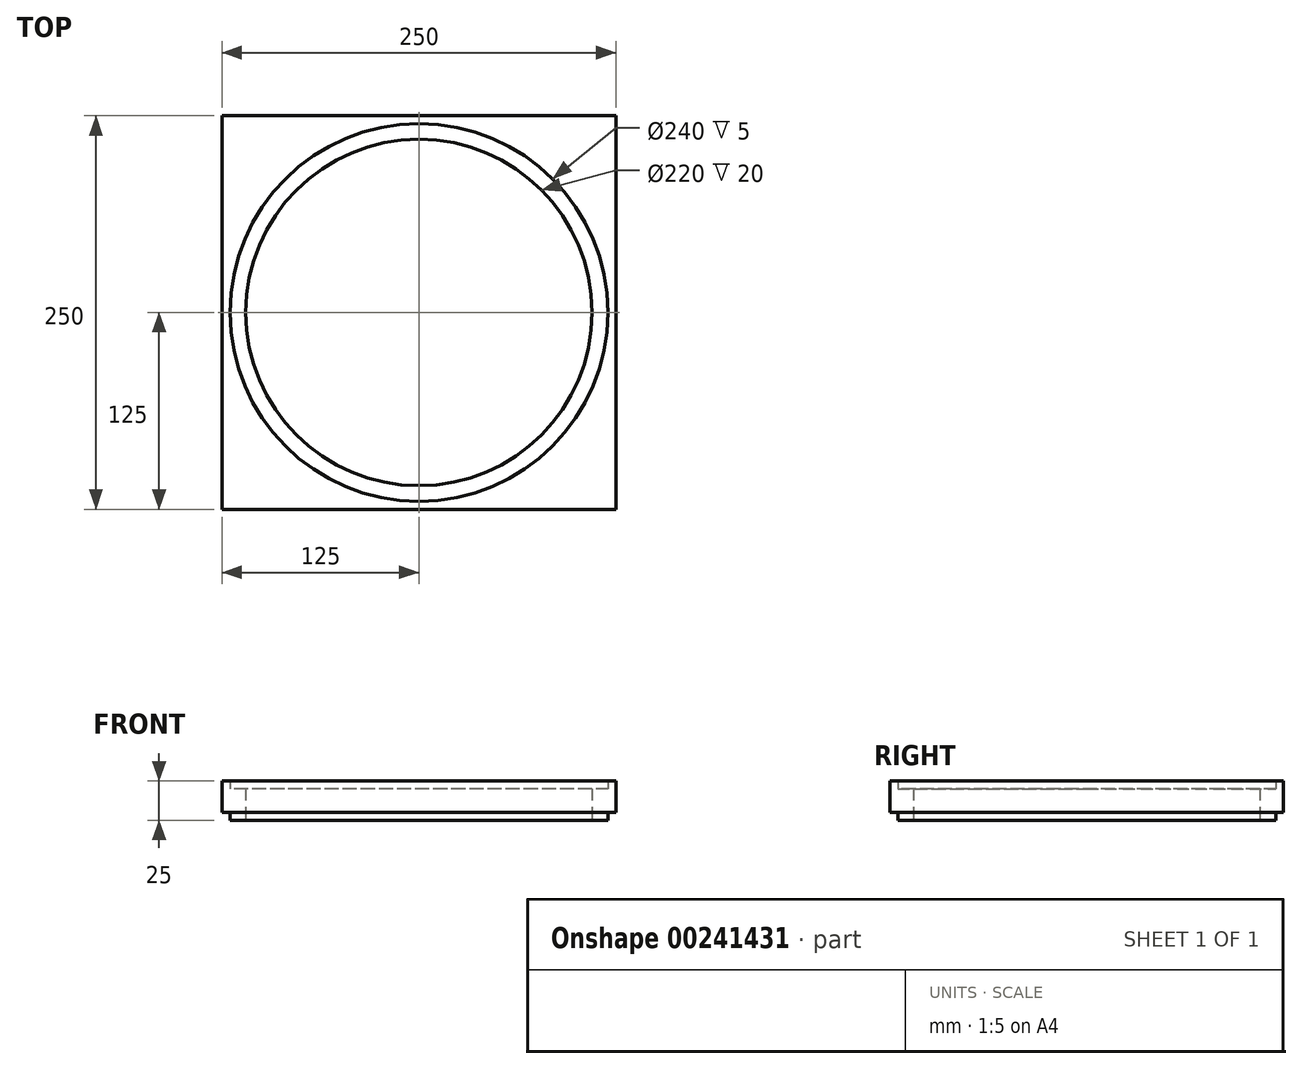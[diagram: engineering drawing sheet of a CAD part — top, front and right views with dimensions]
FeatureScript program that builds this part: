
annotation { "Feature Type Name" : "Feature", "Feature Type Description" : "" }
export const myFeature = defineFeature(function(context is Context, id is Id, definition is map)
    precondition{}
    {
        {
            var Q0;
            Q0=qCreatedBy(makeId("Top.planeOp"),FACE);
            var sketch = newSketch(context, id + "F0", { "sketchPlane" : qUnion([Q0])});
            skLineSegment(sketch, "E0.bottom", {"start": v(-125, 125) * mm, "end": v(125, 125) * mm});
            skLineSegment(sketch, "E0.top", {"start": v(-125, -125) * mm, "end": v(125, -125) * mm});
            skLineSegment(sketch, "E0.left", {"start": v(-125, 125) * mm, "end": v(-125, -125) * mm});
            skLineSegment(sketch, "E0.right", {"start": v(125, 125) * mm, "end": v(125, -125) * mm});
            skPoint(sketch, "E0.middle", {"position": v(0, 0) * mm});
            skCircle(sketch, "E1", {"center": v(0, 0) * mm, "radius": 120 * mm});
            skCircle(sketch, "E2", {"center": v(0, 0) * mm, "radius": 110 * mm});
            skSolve(sketch);
        }
        {
            var Q0;
            Q0 = qSketchRegion(id + "F0", true);
            extrude(context, id + "F1", {"entities" : qUnion([Q0]), "depth" : 20 * mm});
        }
        {
            var Q0;
            Q0=makeQuery(id+"F0.imprint","IMPRINT",FACE,{"disambiguationData":[TD([[makeQuery(id+"F0.imprint","IMPRINT",EDGE,{"derivedFrom":sQuery(id+"F0.wireOp",EDGE,"E1")}),1.0]])]});
            extrude(context, id + "F2", {"entities" : qUnion([Q0]), "operationType" : NewBodyOperationType.ADD, "depth" : 15 * mm, "hasSecondDirection" : true, "secondDirectionOppositeDirection" : true, "secondDirectionDepth" : 5 * mm});
        }
    });
